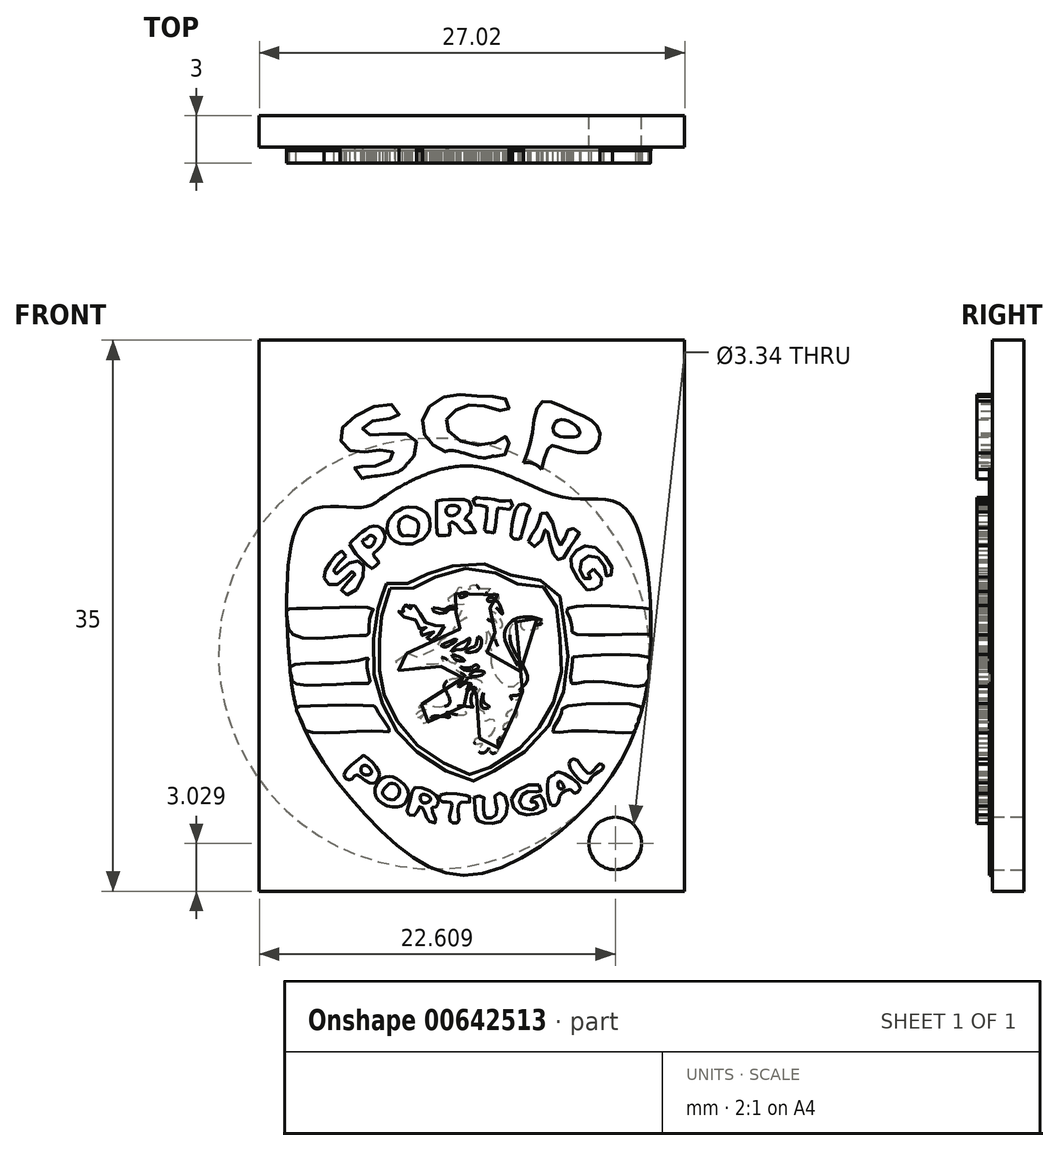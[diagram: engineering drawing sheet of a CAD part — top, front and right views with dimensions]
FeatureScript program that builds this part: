
annotation { "Feature Type Name" : "Feature", "Feature Type Description" : "" }
export const myFeature = defineFeature(function(context is Context, id is Id, definition is map)
    precondition{}
    {
        {
            var Q0;
            Q0=qCreatedBy(makeId("Front.planeOp"),FACE);
            var sketch = newSketch(context, id + "F0", { "sketchPlane" : qUnion([Q0])});
            skLineSegment(sketch, "E0.bottom", {"start": v(-15.43, 13.7) * mm, "end": v(11.59, 13.7) * mm});
            skLineSegment(sketch, "E0.top", {"start": v(-15.43, -21.3) * mm, "end": v(11.59, -21.3) * mm});
            skLineSegment(sketch, "E0.left", {"start": v(-15.43, 13.7) * mm, "end": v(-15.43, -21.3) * mm});
            skPoint(sketch, "E1", {"position": v(11.59, 13.7) * mm});
            skPoint(sketch, "E2", {"position": v(11.59, -21.3) * mm});
            skLineSegment(sketch, "E3", {"start": v(11.59, 13.7) * mm, "end": v(11.59, -21.3) * mm});
            skSolve(sketch);
        }
        {
            var Q0;
            Q0=qCreatedBy(makeId("Front.planeOp"),FACE);
            var sketch = newSketch(context, id + "F1", { "sketchPlane" : qUnion([Q0])});
            skPoint(sketch, "E4.8.internal.snap0", {"position": v(-2.05, -20.29) * mm});
            skFitSpline(sketch, "E4", {"points": [v(-2.05, -20.29) * mm, v(-7.51, -17.64) * mm, v(-12.5, -11.15) * mm, v(-13.53, -6.65) * mm, v(-13.53, 0) * mm, v(-12, 2.96) * mm, v(-8.89, 3.08) * mm, v(-7.39, 3.83) * mm, v(-2.05, 5.7) * mm, v(4.05, 3.69) * mm, v(7.76, 3.09) * mm, v(9.43, -5.8) * mm, v(8.1, -11.92) * mm, v(4.82, -16.5) * mm, v(-2.05, -20.29) * mm]});
            skFitSpline(sketch, "E5", {"points": [v(0, 5.24) * mm, v(-0.48, 6.3) * mm, v(-1.26, 6.22) * mm, v(-3.59, 6.58) * mm, v(-3.52, 5.57) * mm, v(-3.41, 5.6) * mm], "startDerivative": vector(-1.88, 6.53) * mm, "endDerivative": vector(1.52, 1.28) * mm});
            skFitSpline(sketch, "E6", {"points": [v(-5.78, 4.77) * mm, v(-5.98, 5.9) * mm, v(-6.5, 5.4) * mm, v(-8.86, 4.89) * mm, v(-7.39, 3.83) * mm], "startDerivative": vector(-0.76, 7.58) * mm, "endDerivative": vector(8.87, -4.6) * mm});
            skFitSpline(sketch, "E7", {"points": [v(1.07, 4.8) * mm, v(1.36, 5.9) * mm, v(2.48, 5.47) * mm, v(2, 4.39) * mm], "startDerivative": vector(-0.1, 4.46) * mm, "endDerivative": vector(-2.87, -3.44) * mm});
            skFitSpline(sketch, "E8", {"points": [v(-8.86, 4.89) * mm, v(-9.37, 5.65) * mm, v(-8.86, 5.68) * mm, v(-7.7, 5.8) * mm, v(-6.85, 6.44) * mm, v(-7.46, 6.72) * mm, v(-8.86, 6.6) * mm, v(-10.04, 6.93) * mm, v(-10.24, 7.95) * mm, v(-8.86, 9.14) * mm, v(-6.9, 9.55) * mm, v(-6.6, 8.84) * mm, v(-7.8, 8.68) * mm, v(-8.86, 8.1) * mm, v(-8.53, 7.72) * mm, v(-6.6, 7.77) * mm, v(-5.47, 7.33) * mm, v(-5.7, 6.19) * mm, v(-5.98, 5.9) * mm], "startDerivative": vector(-16.53, 19.1) * mm, "endDerivative": vector(-8.11, -5.5) * mm});
            skFitSpline(sketch, "E9", {"points": [v(-3.59, 6.58) * mm, v(-4.82, 7.47) * mm, v(-4.91, 9.07) * mm, v(-3.26, 10.2) * mm, v(-1.08, 10.11) * mm, v(0.3, 9.9) * mm, v(0.33, 9.22) * mm, v(-1.14, 9.53) * mm, v(-2.8, 9.34) * mm, v(-3.59, 8.42) * mm, v(-2.58, 7.26) * mm, v(-0.31, 7.26) * mm, v(0.33, 7.57) * mm, v(0.3, 6.58) * mm, v(-0.48, 6.3) * mm], "startDerivative": vector(-19.26, 9.32) * mm, "endDerivative": vector(-16.98, -0.4) * mm});
            skFitSpline(sketch, "E10", {"points": [v(1.36, 5.9) * mm, v(1.9, 7.72) * mm, v(2.51, 9.77) * mm, v(4.5, 9.16) * mm, v(5.88, 8.42) * mm, v(6.2, 7.38) * mm, v(5.49, 6.58) * mm, v(3.68, 6.86) * mm, v(3.06, 6.98) * mm, v(2.48, 5.47) * mm], "startDerivative": vector(5.01, 12.88) * mm, "endDerivative": vector(-4.42, -17.6) * mm});
            skFitSpline(sketch, "E11", {"points": [v(3.55, 8.6) * mm, v(3.28, 7.84) * mm, v(4.26, 7.53) * mm, v(4.9, 7.72) * mm, v(4.72, 8.2) * mm, v(3.55, 8.6) * mm]});
            skSolve(sketch);
        }
        {
            var Q0;
            Q0 = qSketchRegion(id + "F0", true);
            extrude(context, id + "F2", {"entities" : qUnion([Q0]), "oppositeDirection" : true, "depth" : 2 * mm, "offsetDistance" : 25 * mm});
        }
        {
            var Q0;
            {var subQ0=sQuery(id+"F1.wireOp",EDGE,"E8");Q0=makeQuery(id+"F1.imprint","IMPRINT",FACE,{"disambiguationData":[TD([[makeQuery(id+"F1.imprint","IMPRINT",EDGE,{"derivedFrom":subQ0}),-1.0]])]});}
            var Q1;
            {var subQ0=sQuery(id+"F1.wireOp",EDGE,"E9");Q1=makeQuery(id+"F1.imprint","IMPRINT",FACE,{"disambiguationData":[TD([[makeQuery(id+"F1.imprint","IMPRINT",EDGE,{"derivedFrom":subQ0}),-1.0]])]});}
            var Q2;
            {var subQ0=sQuery(id+"F1.wireOp",EDGE,"E10");Q2=makeQuery(id+"F1.imprint","IMPRINT",FACE,{"disambiguationData":[TD([[makeQuery(id+"F1.imprint","IMPRINT",EDGE,{"derivedFrom":subQ0}),-1.0]])]});}
            extrude(context, id + "F3", {"entities" : qUnion([Q0, Q1, Q2]), "operationType" : NewBodyOperationType.ADD, "depth" : 1 * mm, "offsetDistance" : 25 * mm});
        }
        {
            var Q0;
            {var subQ0=sQuery(id+"F0.wireOp",EDGE,"E0.left");var subQ1=sQuery(id+"F0.wireOp",EDGE,"E0.top");var subQ2=sQuery(id+"F0.wireOp",EDGE,"E0.right");var subQ3=sQuery(id+"F0.wireOp",EDGE,"E0.bottom");Q0=makeQuery(id+"F3.boolean.opBoolean","SPLIT",FACE,{"disambiguationData":[TD([makeQuery(id+"F2.opExtrude","SWEPT_FACE",FACE,{"disambiguationData":[OSD([subQ3])]})])],"derivedFrom":makeQuery(id+"F2.opExtrude","CAP_FACE",FACE,{"disambiguationData":[OSD([subQ3,subQ1,subQ0,subQ2])],"isStart":true})});}
            var sketch = newSketch(context, id + "F4", { "sketchPlane" : qUnion([Q0])});
            skFitSpline(sketch, "E12", {"points": [v(-9.92, 0) * mm, v(-10.21, 0.3) * mm, v(-10.74, -0.17) * mm, v(-11.2, -0.84) * mm, v(-11.3, -1.5) * mm, v(-10.72, -1.9) * mm, v(-9.86, -1.29) * mm, v(-9.46, -1) * mm, v(-9.38, -1.27) * mm, v(-10.21, -2.15) * mm, v(-9.76, -2.47) * mm, v(-8.8, -1.2) * mm, v(-9, -0.4) * mm, v(-9.72, -0.47) * mm, v(-10.37, -1.04) * mm, v(-10.62, -1.14) * mm, v(-10.67, -0.8) * mm, v(-9.92, 0) * mm]});
            skFitSpline(sketch, "E13", {"points": [v(-9.7, 0.77) * mm, v(-8.36, -0.78) * mm, v(-8.28, -0.8) * mm, v(-8.1, -0.67) * mm, v(-7.83, -0.46) * mm, v(-7.94, -0.25) * mm, v(-8.08, -0.13) * mm, v(-8.15, 0) * mm, v(-8.2, 0.08) * mm, v(-7.96, 0.34) * mm, v(-7.75, 0.52) * mm, v(-7.6, 0.72) * mm, v(-7.5, 0.93) * mm, v(-7.44, 1.32) * mm, v(-7.56, 1.59) * mm, v(-7.7, 1.76) * mm, v(-7.92, 1.87) * mm, v(-8.19, 1.9) * mm, v(-8.45, 1.84) * mm, v(-8.63, 1.7) * mm, v(-8.89, 1.53) * mm, v(-8.97, 1.45) * mm, v(-9.18, 1.3) * mm, v(-9.33, 1.13) * mm, v(-9.51, 0.97) * mm, v(-9.7, 0.77) * mm]});
            skFitSpline(sketch, "E14", {"points": [v(-8.87, 0.97) * mm, v(-8.85, 0.82) * mm, v(-8.67, 0.63) * mm, v(-8.56, 0.56) * mm, v(-8.36, 0.57) * mm, v(-8.26, 0.67) * mm, v(-8.16, 0.8) * mm, v(-8.07, 1) * mm, v(-8.07, 1.14) * mm, v(-8.32, 1.29) * mm, v(-8.41, 1.29) * mm, v(-8.54, 1.21) * mm, v(-8.62, 1.05) * mm, v(-8.74, 1.05) * mm, v(-8.8, 1.03) * mm, v(-8.87, 0.97) * mm]});
            skFitSpline(sketch, "E15", {"points": [v(-5.97, 3.09) * mm, v(-6.25, 3.06) * mm, v(-6.48, 2.96) * mm, v(-6.6, 2.82) * mm, v(-6.8, 2.75) * mm, v(-6.9, 2.6) * mm, v(-7.09, 2.47) * mm, v(-7.24, 2.15) * mm, v(-7.28, 2.03) * mm, v(-7.3, 1.82) * mm, v(-7.32, 1.66) * mm, v(-7.26, 1.43) * mm, v(-7.14, 1.2) * mm, v(-6.96, 1.05) * mm, v(-6.76, 0.88) * mm, v(-6.44, 0.77) * mm, v(-6.07, 0.75) * mm, v(-5.66, 0.77) * mm, v(-5.43, 0.89) * mm, v(-5.1, 1.03) * mm, v(-4.86, 1.29) * mm, v(-4.73, 1.4) * mm, v(-4.6, 1.72) * mm, v(-4.58, 2.03) * mm, v(-4.61, 2.34) * mm, v(-4.77, 2.68) * mm, v(-5.04, 2.88) * mm, v(-5.35, 3.03) * mm, v(-5.97, 3.09) * mm]});
            skFitSpline(sketch, "E16", {"points": [v(-6.06, 2.53) * mm, v(-6.5, 2.25) * mm, v(-6.57, 1.99) * mm, v(-6.55, 1.59) * mm, v(-6.34, 1.29) * mm, v(-5.88, 1.29) * mm, v(-5.47, 1.29) * mm, v(-5.33, 1.77) * mm, v(-5.34, 2.1) * mm, v(-5.61, 2.35) * mm, v(-5.97, 2.5) * mm, v(-6.06, 2.53) * mm]});
            skFitSpline(sketch, "E17", {"points": [v(-4.18, 3.5) * mm, v(-4.06, 1.29) * mm, v(-3.97, 1.29) * mm, v(-3.89, 1.29) * mm], "startDerivative": vector(-0.03, -4.4) * mm, "endDerivative": vector(0.58, -0.07) * mm});
            skFitSpline(sketch, "E18", {"points": [v(-3.89, 1.29) * mm, v(-3.59, 1.29) * mm, v(-3.4, 1.29) * mm, v(-3.3, 1.66) * mm, v(-3.38, 2.1) * mm, v(-3.16, 2.15) * mm, v(-2.81, 1.87) * mm, v(-2.45, 1.45) * mm, v(-2.13, 1.47) * mm, v(-1.7, 1.47) * mm, v(-1.79, 1.7) * mm, v(-1.96, 1.94) * mm, v(-2.13, 2.18) * mm, v(-2.38, 2.31) * mm, v(-2.28, 2.5) * mm, v(-2, 2.75) * mm, v(-2.02, 3.27) * mm, v(-2.22, 3.53) * mm, v(-2.99, 3.58) * mm, v(-3.69, 3.57) * mm, v(-4.18, 3.5) * mm], "startDerivative": vector(6.92, 0.45) * mm, "endDerivative": vector(-8.3, -1.8) * mm});
            skFitSpline(sketch, "E19", {"points": [v(-3.47, 3.09) * mm, v(-3.46, 2.6) * mm, v(-2.86, 2.69) * mm, v(-2.78, 3.09) * mm, v(-3.47, 3.09) * mm]});
            skFitSpline(sketch, "E20", {"points": [v(-0.97, 3.09) * mm, v(-1.13, 1.59) * mm, v(-1.03, 1.52) * mm, v(-0.98, 1.51) * mm, v(-0.86, 1.51) * mm, v(-0.77, 1.5) * mm, v(-0.7, 1.48) * mm, v(-0.6, 1.47) * mm, v(-0.56, 1.47) * mm, v(-0.5, 1.47) * mm, v(-0.3, 3.09) * mm, v(-0.24, 3.01) * mm, v(0.16, 3) * mm, v(0.6, 2.99) * mm, v(0.6, 3.5) * mm, v(0.31, 3.5) * mm, v(-0.13, 3.5) * mm, v(-0.49, 3.58) * mm, v(-1, 3.64) * mm, v(-1.36, 3.66) * mm, v(-1.79, 3.68) * mm, v(-1.8, 3.31) * mm, v(-1.5, 3.17) * mm, v(-0.97, 3.09) * mm]});
            skFitSpline(sketch, "E21", {"points": [v(1.07, 3.23) * mm, v(0.57, 1.58) * mm, v(0.55, 1.29) * mm, v(0.63, 1.17) * mm, v(0.78, 1.05) * mm, v(0.96, 1.05) * mm, v(1.1, 1.05) * mm, v(1.22, 1.29) * mm, v(1.33, 1.69) * mm, v(1.45, 2.16) * mm, v(1.67, 2.8) * mm, v(1.76, 3.09) * mm, v(1.07, 3.23) * mm]});
            skFitSpline(sketch, "E22", {"points": [v(1.66, 0.9) * mm, v(2.01, 1.5) * mm, v(2.35, 2.22) * mm, v(2.52, 2.73) * mm, v(3.02, 2.51) * mm, v(3.66, 0.7) * mm, v(4.07, 1.37) * mm, v(4.34, 1.76) * mm, v(4.89, 1.47) * mm, v(4.57, 0.98) * mm, v(3.78, -0.23) * mm, v(3.44, -0.16) * mm, v(3.07, 0.72) * mm, v(2.76, 1.71) * mm, v(2.23, 0.62) * mm, v(1.66, 0.9) * mm]});
            skFitSpline(sketch, "E23", {"points": [v(5.8, -0.84) * mm, v(6.39, -1.76) * mm, v(6.13, -1.9) * mm, v(5.64, -2.25) * mm, v(4.58, -1.13) * mm, v(4.34, -0.18) * mm, v(4.84, 0.44) * mm, v(5.7, 0.62) * mm, v(6.85, -0.5) * mm, v(6.96, -1.16) * mm, v(6.67, -1.35) * mm, v(6.49, -0.64) * mm, v(5.8, 0) * mm, v(5.1, -0.23) * mm, v(4.94, -0.9) * mm, v(5.33, -1.52) * mm, v(5.62, -1.4) * mm, v(5.47, -1.1) * mm, v(5.8, -0.84) * mm]});
            skFitSpline(sketch, "E24", {"points": [v(-10.06, -13.92) * mm, v(-8.9, -12.76) * mm, v(-8.8, -12.68) * mm, v(-7.95, -13.48) * mm, v(-7.85, -14.11) * mm, v(-8.34, -14.46) * mm, v(-9.26, -13.92) * mm, v(-9.64, -14.22) * mm, v(-10.06, -13.92) * mm]});
            skFitSpline(sketch, "E25", {"points": [v(-8.78, -13.31) * mm, v(-8.3, -13.7) * mm, v(-8.57, -13.93) * mm, v(-8.98, -13.66) * mm, v(-8.78, -13.31) * mm]});
            skFitSpline(sketch, "E26", {"points": [v(-7.16, -14) * mm, v(-6.52, -14.3) * mm, v(-6, -14.83) * mm, v(-6.09, -15.59) * mm, v(-6.73, -15.97) * mm, v(-7.8, -15.6) * mm, v(-8.1, -14.9) * mm, v(-7.77, -14.25) * mm, v(-7.16, -14) * mm]});
            skFitSpline(sketch, "E27", {"points": [v(-7.37, -14.67) * mm, v(-7.04, -14.44) * mm, v(-6.55, -14.76) * mm, v(-6.68, -15.34) * mm, v(-7.2, -15.47) * mm, v(-7.61, -15.04) * mm, v(-7.37, -14.67) * mm]});
            skFitSpline(sketch, "E28", {"points": [v(-5.54, -14.73) * mm, v(-4.23, -15.17) * mm, v(-4.06, -15.61) * mm, v(-4.22, -15.96) * mm, v(-4.48, -16.03) * mm, v(-4.2, -16.92) * mm, v(-4.72, -16.8) * mm, v(-4.92, -16.23) * mm, v(-5.25, -15.93) * mm, v(-5.54, -16.47) * mm, v(-6.04, -16.34) * mm, v(-5.86, -15.63) * mm, v(-5.54, -14.73) * mm]});
            skFitSpline(sketch, "E29", {"points": [v(-5.1, -15.17) * mm, v(-4.56, -15.38) * mm, v(-4.73, -15.66) * mm, v(-5.15, -15.59) * mm, v(-5.1, -15.17) * mm]});
            skFitSpline(sketch, "E30", {"points": [v(-3.93, -15.2) * mm, v(-2.06, -15.31) * mm, v(-2.07, -15.38) * mm, v(-2.07, -15.66) * mm, v(-2.63, -15.66) * mm, v(-2.79, -16.42) * mm, v(-2.8, -16.92) * mm, v(-3.28, -16.92) * mm, v(-3.26, -16.13) * mm, v(-3.26, -15.66) * mm, v(-3.85, -15.61) * mm, v(-3.93, -15.2) * mm]});
            skFitSpline(sketch, "E31", {"points": [v(-1.8, -15.34) * mm, v(-1.19, -15.31) * mm, v(-1.19, -15.66) * mm, v(-1.16, -16.33) * mm, v(-1.04, -16.63) * mm, v(-0.46, -16.54) * mm, v(-0.37, -15.96) * mm, v(-0.41, -15.18) * mm, v(0.1, -15.17) * mm, v(0.12, -16.69) * mm, v(-1.01, -16.99) * mm, v(-1.66, -16.67) * mm, v(-1.74, -15.66) * mm, v(-1.8, -15.34) * mm]});
            skFitSpline(sketch, "E32", {"points": [v(2.32, -14.56) * mm, v(2.42, -14.98) * mm, v(1.75, -14.94) * mm, v(1.17, -15.34) * mm, v(1.22, -15.96) * mm, v(2.2, -16.01) * mm, v(2.18, -15.66) * mm, v(1.86, -15.66) * mm, v(1.85, -15.46) * mm, v(2.52, -15.23) * mm, v(2.63, -15.66) * mm, v(2.8, -16.09) * mm, v(1.67, -16.44) * mm, v(0.82, -16.14) * mm, v(0.69, -15.14) * mm, v(2.32, -14.56) * mm]});
            skFitSpline(sketch, "E33", {"points": [v(3.13, -15.86) * mm, v(2.98, -14.08) * mm, v(3.28, -13.93) * mm, v(3.48, -13.74) * mm, v(4.95, -14.73) * mm, v(4.56, -15.08) * mm, v(4.34, -14.84) * mm, v(3.66, -15.24) * mm, v(3.58, -15.66) * mm, v(3.13, -15.86) * mm]});
            skFitSpline(sketch, "E34", {"points": [v(3.58, -14.73) * mm, v(3.9, -14.73) * mm, v(3.63, -14.33) * mm, v(3.58, -14.73) * mm]});
            skFitSpline(sketch, "E35", {"points": [v(4.25, -13.22) * mm, v(5.3, -14.44) * mm, v(5.74, -14) * mm, v(6.42, -13.45) * mm, v(6.21, -13.21) * mm, v(5.52, -13.84) * mm, v(4.67, -12.94) * mm, v(4.25, -13.22) * mm]});
            skSolve(sketch);
        }
        {
            var Q0;
            Q0 = qSketchRegion(id + "F4", true);
            extrude(context, id + "F5", {"entities" : qUnion([Q0]), "operationType" : NewBodyOperationType.ADD, "depth" : 1 * mm, "offsetDistance" : 25 * mm});
        }
        {
            var Q0;
            {var subQ3=sQuery(id+"F0.wireOp",EDGE,"E0.left");var subQ7=sQuery(id+"F0.wireOp",EDGE,"E0.top");var subQ11=sQuery(id+"F0.wireOp",EDGE,"E0.right");var subQ14=sQuery(id+"F0.wireOp",EDGE,"E0.bottom");var subQ15=makeQuery(id+"F2.opExtrude","SWEPT_FACE",FACE,{"disambiguationData":[OSD([subQ14])]});Q0=makeQuery(id+"F5.boolean.opBoolean","SPLIT",FACE,{"disambiguationData":[TD([subQ15])],"derivedFrom":makeQuery(id+"F3.boolean.opBoolean","SPLIT",FACE,{"disambiguationData":[TD([subQ15])],"derivedFrom":makeQuery(id+"F2.opExtrude","CAP_FACE",FACE,{"disambiguationData":[OSD([subQ14,subQ7,subQ3,subQ11])],"isStart":true})})});}
            var sketch = newSketch(context, id + "F6", { "sketchPlane" : qUnion([Q0])});
            skFitSpline(sketch, "E36", {"points": [v(-12.36, -3.34) * mm, v(-8.22, -3.38) * mm, v(-8.4, -3.83) * mm, v(-8.48, -4.95) * mm, v(-9.02, -5.05) * mm, v(-13.26, -5.03) * mm, v(-13.66, -3.98) * mm, v(-13.68, -3.47) * mm, v(-12.36, -3.34) * mm]});
            skFitSpline(sketch, "E37", {"points": [v(-9.84, -6.75) * mm, v(-8.5, -6.52) * mm, v(-8.62, -6.84) * mm, v(-8.4, -8) * mm, v(-9.06, -8.11) * mm, v(-13.22, -8.1) * mm, v(-13.41, -7.58) * mm, v(-13.46, -7.02) * mm, v(-9.84, -6.75) * mm]});
            skFitSpline(sketch, "E38", {"points": [v(-12.88, -9.58) * mm, v(-8.03, -9.58) * mm, v(-8.01, -9.7) * mm, v(-7.15, -11.09) * mm, v(-7.87, -11.13) * mm, v(-12.38, -11.15) * mm, v(-12.68, -10.67) * mm, v(-13.04, -9.86) * mm, v(-13.08, -9.68) * mm, v(-12.88, -9.58) * mm]});
            skFitSpline(sketch, "E39", {"points": [v(4.14, -3.35) * mm, v(9.36, -3.37) * mm, v(9.41, -3.46) * mm, v(9.41, -4.99) * mm, v(9.26, -4.99) * mm, v(4.52, -4.92) * mm, v(4.44, -4.6) * mm, v(4.37, -4.21) * mm, v(4.25, -3.83) * mm, v(4.14, -3.35) * mm]});
            skFitSpline(sketch, "E40", {"points": [v(9.33, -6.47) * mm, v(4.47, -6.44) * mm, v(4.47, -6.55) * mm, v(4.36, -8.04) * mm, v(5.04, -8.04) * mm, v(7.43, -8.15) * mm, v(9.23, -8.1) * mm, v(9.28, -7.17) * mm, v(9.28, -7.07) * mm, v(9.33, -6.82) * mm, v(9.33, -6.47) * mm]});
            skFitSpline(sketch, "E41", {"points": [v(8.86, -9.58) * mm, v(3.86, -9.63) * mm, v(3.79, -9.82) * mm, v(3.66, -10.24) * mm, v(3.2, -11.16) * mm, v(4.5, -11.1) * mm, v(8.32, -11.2) * mm, v(8.49, -10.97) * mm, v(8.51, -10.73) * mm, v(8.67, -10.58) * mm, v(8.65, -10.44) * mm, v(8.67, -10.25) * mm, v(8.74, -10.15) * mm, v(8.82, -9.97) * mm, v(8.83, -9.86) * mm, v(8.86, -9.58) * mm]});
            skSolve(sketch);
        }
        {
            var Q0;
            Q0=makeQuery(id+"F6.imprint","IMPRINT",FACE,{"disambiguationData":[TD([[makeQuery(id+"F6.imprint","IMPRINT",EDGE,{"derivedFrom":sQuery(id+"F6.wireOp",EDGE,"E38")}),-1.0]])]});
            var Q1;
            {var subQ0=sQuery(id+"F6.wireOp",EDGE,"E37");var subQ1=makeQuery(id+"F2.opExtrude","CAP_EDGE",EDGE,{"disambiguationData":[OSD([sQuery(id+"F0.wireOp",EDGE,"E0.left")])],"isStart":true});var subQ2=makeQuery(id+"F6.imprint","INTERSECT",VERTEX,{"disambiguationData":[OD(0.0)],"derivedFrom":[subQ1,subQ0]});Q1=makeQuery(id+"F6.imprint","IMPRINT",FACE,{"disambiguationData":[TD([[makeQuery(id+"F6.imprint","IMPRINT",EDGE,{"disambiguationData":[TD([[subQ2,1.0]])],"derivedFrom":subQ0}),-1.0]])]});}
            var Q2;
            {var subQ0=sQuery(id+"F6.wireOp",EDGE,"E36");var subQ1=makeQuery(id+"F2.opExtrude","CAP_EDGE",EDGE,{"disambiguationData":[OSD([sQuery(id+"F0.wireOp",EDGE,"E0.left")])],"isStart":true});var subQ2=makeQuery(id+"F6.imprint","INTERSECT",VERTEX,{"disambiguationData":[OD(0.0)],"derivedFrom":[subQ1,subQ0]});Q2=makeQuery(id+"F6.imprint","IMPRINT",FACE,{"disambiguationData":[TD([[makeQuery(id+"F6.imprint","IMPRINT",EDGE,{"disambiguationData":[TD([[subQ2,-1.0]])],"derivedFrom":subQ0}),-1.0]])]});}
            var Q3;
            Q3=makeQuery(id+"F6.imprint","IMPRINT",FACE,{"disambiguationData":[TD([[makeQuery(id+"F6.imprint","IMPRINT",EDGE,{"derivedFrom":sQuery(id+"F6.wireOp",EDGE,"E40")}),1.0]])]});
            var Q4;
            Q4=makeQuery(id+"F6.imprint","IMPRINT",FACE,{"disambiguationData":[TD([[makeQuery(id+"F6.imprint","IMPRINT",EDGE,{"derivedFrom":sQuery(id+"F6.wireOp",EDGE,"E41")}),1.0]])]});
            var Q5;
            Q5=makeQuery(id+"F6.imprint","IMPRINT",FACE,{"disambiguationData":[TD([[makeQuery(id+"F6.imprint","IMPRINT",EDGE,{"derivedFrom":sQuery(id+"F6.wireOp",EDGE,"E39")}),-1.0]])]});
            extrude(context, id + "F7", {"entities" : qUnion([Q0, Q1, Q2, Q3, Q4, Q5]), "operationType" : NewBodyOperationType.ADD, "depth" : 1 * mm, "offsetDistance" : 25 * mm});
        }
        {
            var Q0;
            {var subQ3=sQuery(id+"F0.wireOp",EDGE,"E0.left");var subQ18=sQuery(id+"F0.wireOp",EDGE,"E0.top");var subQ23=sQuery(id+"F0.wireOp",EDGE,"E0.right");var subQ27=sQuery(id+"F0.wireOp",EDGE,"E0.bottom");var subQ28=makeQuery(id+"F2.opExtrude","SWEPT_FACE",FACE,{"disambiguationData":[OSD([subQ27])]});Q0=makeQuery(id+"F7.boolean.opBoolean","SPLIT",FACE,{"disambiguationData":[TD([subQ28])],"derivedFrom":makeQuery(id+"F5.boolean.opBoolean","SPLIT",FACE,{"disambiguationData":[TD([subQ28])],"derivedFrom":makeQuery(id+"F3.boolean.opBoolean","SPLIT",FACE,{"disambiguationData":[TD([subQ28])],"derivedFrom":makeQuery(id+"F2.opExtrude","CAP_FACE",FACE,{"disambiguationData":[OSD([subQ27,subQ18,subQ3,subQ23])],"isStart":true})})})});}
            var sketch = newSketch(context, id + "F8", { "sketchPlane" : qUnion([Q0])});
            skFitSpline(sketch, "E42", {"points": [v(-7.37, -1.77) * mm, v(-6.23, -1.77) * mm, v(-5.05, -1.31) * mm, v(-3.57, -0.74) * mm, v(-0.95, -0.55) * mm, v(1.03, -1.39) * mm, v(3.23, -1.85) * mm, v(3.88, -4) * mm, v(4.18, -6.21) * mm, v(3.6, -9.55) * mm, v(1.6, -12.29) * mm, v(-1.02, -13.96) * mm, v(-2.05, -14.3) * mm, v(-4.63, -13) * mm, v(-6.42, -11.5) * mm, v(-7.63, -9.33) * mm, v(-8.2, -6.86) * mm, v(-7.97, -3.7) * mm, v(-7.7, -2.76) * mm, v(-7.6, -2.41) * mm, v(-7.55, -2.15) * mm, v(-7.37, -1.77) * mm]});
            skFitSpline(sketch, "E43", {"points": [v(-7.14, -2.1) * mm, v(-5.93, -2.07) * mm, v(-4.85, -1.68) * mm, v(-3.23, -0.95) * mm, v(-0.98, -0.91) * mm, v(0.32, -1.45) * mm, v(1.59, -1.95) * mm, v(2.94, -2.07) * mm, v(3.5, -3.58) * mm, v(3.72, -5.86) * mm, v(3.66, -8.18) * mm, v(2.85, -10.07) * mm, v(1.92, -11.4) * mm, v(0.34, -12.79) * mm, v(-1.66, -13.84) * mm, v(-2.1, -13.9) * mm, v(-3.78, -13.15) * mm, v(-5.48, -11.95) * mm, v(-6.86, -10.2) * mm, v(-7.58, -8.6) * mm, v(-7.79, -7.32) * mm, v(-7.8, -5.46) * mm, v(-7.75, -4.24) * mm, v(-7.4, -2.91) * mm, v(-7.32, -2.69) * mm, v(-7.29, -2.48) * mm, v(-7.22, -2.3) * mm, v(-7.14, -2.1) * mm]});
            skSolve(sketch);
        }
        {
            var Q0;
            Q0=makeQuery(id+"F8.imprint","IMPRINT",FACE,{"disambiguationData":[TD([[makeQuery(id+"F8.imprint","IMPRINT",EDGE,{"derivedFrom":sQuery(id+"F8.wireOp",EDGE,"E42")}),-1.0]])]});
            extrude(context, id + "F9", {"entities" : qUnion([Q0]), "operationType" : NewBodyOperationType.ADD, "depth" : 1 * mm, "offsetDistance" : 25 * mm});
        }
        {
            var Q0;
            {var subQ3=sQuery(id+"F0.wireOp",EDGE,"E0.left");var subQ20=sQuery(id+"F0.wireOp",EDGE,"E0.top");var subQ26=sQuery(id+"F0.wireOp",EDGE,"E0.right");var subQ30=sQuery(id+"F0.wireOp",EDGE,"E0.bottom");var subQ31=makeQuery(id+"F2.opExtrude","SWEPT_FACE",FACE,{"disambiguationData":[OSD([subQ30])]});Q0=makeQuery(id+"F9.boolean.opBoolean","SPLIT",FACE,{"disambiguationData":[TD([subQ31])],"derivedFrom":makeQuery(id+"F7.boolean.opBoolean","SPLIT",FACE,{"disambiguationData":[TD([subQ31])],"derivedFrom":makeQuery(id+"F5.boolean.opBoolean","SPLIT",FACE,{"disambiguationData":[TD([subQ31])],"derivedFrom":makeQuery(id+"F3.boolean.opBoolean","SPLIT",FACE,{"disambiguationData":[TD([subQ31])],"derivedFrom":makeQuery(id+"F2.opExtrude","CAP_FACE",FACE,{"disambiguationData":[OSD([subQ30,subQ20,subQ3,subQ26])],"isStart":true})})})})});}
            var sketch = newSketch(context, id + "F10", { "sketchPlane" : qUnion([Q0])});
            skFitSpline(sketch, "E44", {"points": [v(-3.67, -4.45) * mm, v(-4.36, -4.42) * mm, v(-5, -4.1) * mm, v(-5.38, -3.37) * mm, v(-5.72, -3.12) * mm, v(-5.87, -3.12) * mm, v(-5.73, -3.38) * mm, v(-5.96, -3.23) * mm, v(-6.15, -3.14) * mm, v(-6.38, -3.23) * mm, v(-6.13, -3.52) * mm, v(-6.38, -3.54) * mm, v(-6.57, -3.48) * mm, v(-6.49, -3.77) * mm, v(-5.6, -4.03) * mm, v(-5.27, -4.4) * mm, v(-5.4, -4.52) * mm, v(-5.29, -4.63) * mm, v(-4.9, -4.54) * mm, v(-4.8, -4.62) * mm, v(-5.29, -4.9) * mm, v(-5.12, -5.06) * mm, v(-4.67, -4.94) * mm, v(-4.5, -4.8) * mm, v(-4.35, -4.83) * mm, v(-4.8, -5.25) * mm, v(-4.6, -5.37) * mm, v(-4.14, -5.14) * mm, v(-3.67, -4.45) * mm]});
            skFitSpline(sketch, "E45", {"points": [v(-2.96, -2.4) * mm, v(-3.47, -2.55) * mm, v(-3.5, -2.73) * mm, v(-3.35, -2.78) * mm, v(-3.45, -2.9) * mm, v(-3.45, -3.07) * mm, v(-3.08, -3.06) * mm, v(-2.56, -3.01) * mm, v(-2.21, -3.38) * mm, v(-2.7, -3.63) * mm, v(-3.11, -3.63) * mm, v(-2.85, -4.07) * mm, v(-2.5, -3.86) * mm, v(-2.24, -3.9) * mm, v(-2.34, -4.07) * mm, v(-2.59, -4.2) * mm, v(-3.3, -4.52) * mm, v(-3.3, -4.66) * mm, v(-3.02, -4.66) * mm, v(-2.68, -4.64) * mm, v(-3.28, -4.97) * mm, v(-3.94, -5.35) * mm, v(-4.01, -5.71) * mm, v(-4.1, -5.83) * mm, v(-4.79, -6.2) * mm, v(-5.4, -6.47) * mm, v(-5.9, -6.33) * mm, v(-6.3, -6.1) * mm, v(-6.56, -6.22) * mm, v(-6.3, -6.38) * mm, v(-6.18, -6.53) * mm, v(-6.68, -6.64) * mm, v(-6.79, -6.89) * mm, v(-6.57, -6.87) * mm, v(-6.28, -6.78) * mm, v(-6.2, -6.89) * mm, v(-6.43, -7) * mm, v(-6.56, -7.37) * mm, v(-6.18, -7.3) * mm, v(-5.63, -7.01) * mm, v(-5.1, -6.95) * mm, v(-4.74, -7.1) * mm, v(-4.62, -7) * mm, v(-4.85, -6.8) * mm, v(-4.77, -6.66) * mm, v(-4.3, -6.87) * mm, v(-3.64, -7.01) * mm, v(-3.73, -6.8) * mm, v(-4.17, -6.58) * mm, v(-3.81, -6.46) * mm, v(-3.16, -6.78) * mm, v(-2.93, -6.8) * mm, v(-3.08, -7.06) * mm, v(-2.35, -7.63) * mm, v(-2.56, -7.77) * mm, v(-3.25, -7.85) * mm, v(-3.69, -8.2) * mm, v(-3.4, -8.97) * mm, v(-3.4, -9.43) * mm, v(-4.15, -9.62) * mm, v(-4.76, -9.45) * mm, v(-5.2, -9.48) * mm, v(-5.32, -9.64) * mm, v(-4.87, -9.67) * mm, v(-4.9, -9.82) * mm, v(-5.2, -9.85) * mm, v(-5.5, -10.15) * mm, v(-5.46, -10.32) * mm, v(-4.98, -10.05) * mm, v(-5.27, -10.47) * mm, v(-4.73, -10.57) * mm, v(-4.35, -10.18) * mm, v(-3.33, -10.24) * mm, v(-3.53, -9.96) * mm, v(-2.71, -10.12) * mm, v(-2.28, -9.98) * mm, v(-2.76, -9.7) * mm, v(-2.83, -9.54) * mm, v(-1.84, -9.6) * mm, v(-1.95, -9.42) * mm, v(-1.83, -8.63) * mm, v(-1.66, -8.46) * mm, v(-1.76, -8.36) * mm, v(-2.07, -8.46) * mm, v(-2.18, -8.61) * mm, v(-2.26, -8.52) * mm, v(-2.1, -8.3) * mm, v(-1.97, -8.15) * mm, v(-2.35, -8.12) * mm, v(-2.63, -8.3) * mm, v(-2.8, -8.29) * mm, v(-2.66, -8.07) * mm, v(-2.3, -7.96) * mm, v(-2.18, -7.77) * mm, v(-1.72, -7.79) * mm, v(-1.27, -8.04) * mm, v(-1.45, -8.47) * mm, v(-1.69, -9.08) * mm, v(-1.48, -9.71) * mm, v(-1.13, -10) * mm, v(-1.13, -10.5) * mm, v(-0.72, -10.33) * mm, v(-0.45, -10.72) * mm, v(-0.94, -11.57) * mm, v(-1.55, -11.59) * mm, v(-1.8, -11.73) * mm, v(-1.69, -11.93) * mm, v(-1.27, -11.93) * mm, v(-1.5, -12.37) * mm, v(-1.13, -12.5) * mm, v(-0.83, -12.2) * mm, v(-0.72, -12.49) * mm, v(-0.34, -12.46) * mm, v(-0.23, -12.13) * mm, v(-0.26, -11.68) * mm, v(0.27, -11.19) * mm, v(0.31, -10.95) * mm, v(0.11, -11.03) * mm, v(0.14, -10.7) * mm, v(0.6, -10.46) * mm, v(0.97, -10.15) * mm, v(0.94, -9.85) * mm, v(0.66, -10.07) * mm, v(0.28, -10.2) * mm, v(0.36, -9.91) * mm, v(1.01, -9.48) * mm, v(1.1, -9.08) * mm, v(0.81, -9.2) * mm, v(0.52, -8.92) * mm, v(0.9, -8.86) * mm, v(1.3, -8.61) * mm, v(1.1, -8.55) * mm, v(1.52, -8.07) * mm, v(1.37, -7.08) * mm, v(0.62, -5.79) * mm, v(0.49, -5.03) * mm, v(0.66, -4.36) * mm, v(1.12, -4.16) * mm, v(1.15, -4.44) * mm, v(1.5, -4.73) * mm, v(2.11, -4.64) * mm, v(2.3, -4.55) * mm, v(2.2, -4.4) * mm, v(2.5, -4.31) * mm, v(2.32, -4.16) * mm, v(2.56, -4.1) * mm, v(2.22, -3.97) * mm, v(1.85, -3.88) * mm, v(1.25, -3.9) * mm, v(0.64, -4.13) * mm, v(0.16, -4.84) * mm, v(0.38, -5.87) * mm, v(1.12, -7.26) * mm, v(1.12, -7.87) * mm, v(0.6, -8.36) * mm, v(-0.2, -7.9) * mm, v(-0.68, -6.87) * mm, v(-0.7, -5.9) * mm, v(-0.79, -5.82) * mm, v(-0.97, -6.16) * mm, v(-1.03, -5.7) * mm, v(-0.96, -4.98) * mm, v(-1.07, -4.62) * mm, v(-0.83, -4.9) * mm, v(-0.63, -5.56) * mm, v(-0.3, -5.74) * mm, v(-0.4, -5.48) * mm, v(-0.45, -4.67) * mm, v(-0.62, -4.2) * mm, v(-0.93, -4.04) * mm, v(-0.55, -3.97) * mm, v(-0.23, -4.53) * mm, v(0, -4.52) * mm, v(-0.2, -3.88) * mm, v(-0.68, -3.5) * mm, v(-0.79, -3.3) * mm, v(-0.5, -3.23) * mm, v(0, -3.7) * mm, v(-0.18, -3.1) * mm, v(-0.4, -2.87) * mm, v(-0.86, -2.89) * mm, v(-0.94, -2.8) * mm, v(-0.82, -2.64) * mm, v(-0.23, -2.75) * mm, v(-0.38, -2.42) * mm, v(-1.08, -2.42) * mm, v(-0.8, -2.14) * mm, v(-1.45, -2.1) * mm, v(-1.58, -1.91) * mm, v(-2.06, -1.97) * mm, v(-2.06, -2.14) * mm, v(-2.77, -2.03) * mm, v(-2.96, -2.4) * mm]});
            skFitSpline(sketch, "E46", {"points": [v(-4.4, -3.32) * mm, v(-4.26, -3.57) * mm, v(-3.52, -3.57) * mm, v(-3.33, -3.38) * mm, v(-2.88, -3.37) * mm, v(-3.02, -3.28) * mm, v(-3.45, -3.26) * mm, v(-3.66, -3.42) * mm, v(-4.4, -3.32) * mm]});
            skFitSpline(sketch, "E47", {"points": [v(-3.27, -6.1) * mm, v(-2.93, -5.97) * mm, v(-2.42, -5.9) * mm, v(-2.06, -5.25) * mm, v(-2.4, -5.43) * mm, v(-2.82, -5.65) * mm, v(-3.27, -6.1) * mm]});
            skFitSpline(sketch, "E48", {"points": [v(-2.9, -5.3) * mm, v(-3.86, -5.7) * mm, v(-3.75, -5.77) * mm, v(-3.36, -5.7) * mm, v(-2.9, -5.3) * mm]});
            skFitSpline(sketch, "E49", {"points": [v(-2.34, -6.05) * mm, v(-1.84, -5.79) * mm, v(-1.64, -5.65) * mm, v(-1.55, -5.17) * mm, v(-1.36, -5.25) * mm, v(-1.42, -5.87) * mm, v(-2.09, -6.15) * mm, v(-2.34, -6.05) * mm]});
            skFitSpline(sketch, "E50", {"points": [v(-3.18, -6.28) * mm, v(-2.4, -6.64) * mm, v(-2.79, -6.66) * mm, v(-3.07, -6.5) * mm, v(-3.18, -6.28) * mm]});
            skFitSpline(sketch, "E51", {"points": [v(-2.66, -7.06) * mm, v(-2.28, -7.14) * mm, v(-1.83, -7) * mm, v(-1.69, -6.92) * mm, v(-1.5, -7.04) * mm, v(-2.17, -7.3) * mm, v(-2.66, -7.06) * mm]});
            skFitSpline(sketch, "E52", {"points": [v(-2.06, -7.6) * mm, v(-1.47, -7.63) * mm, v(-1.14, -7.39) * mm, v(-1.78, -7.36) * mm, v(-2.06, -7.6) * mm]});
            skFitSpline(sketch, "E53", {"points": [v(-1.2, -8.72) * mm, v(-1.2, -9.25) * mm, v(-0.82, -9.59) * mm, v(-1.14, -9.7) * mm, v(-1.36, -9.34) * mm, v(-1.2, -8.72) * mm]});
            skFitSpline(sketch, "E54", {"points": [v(-2.66, -2.64) * mm, v(-2.17, -2.4) * mm, v(-2.65, -2.4) * mm, v(-2.66, -2.64) * mm]});
            skSolve(sketch);
        }
        {
            var Q0;
            Q0=makeQuery(id+"F10.imprint","IMPRINT",FACE,{"disambiguationData":[TD([[makeQuery(id+"F10.imprint","IMPRINT",EDGE,{"derivedFrom":sQuery(id+"F10.wireOp",EDGE,"E45")}),1.0]])]});
            var Q1;
            Q1=makeQuery(id+"F10.imprint","IMPRINT",FACE,{"disambiguationData":[TD([[makeQuery(id+"F10.imprint","IMPRINT",EDGE,{"derivedFrom":sQuery(id+"F10.wireOp",EDGE,"E44")}),1.0]])]});
            var Q2;
            Q2=makeQuery(id+"F10.imprint","IMPRINT",FACE,{"disambiguationData":[TD([[makeQuery(id+"F10.imprint","IMPRINT",EDGE,{"derivedFrom":sQuery(id+"F10.wireOp",EDGE,"E46")}),1.0]])]});
            extrude(context, id + "F11", {"entities" : qUnion([Q0, Q1, Q2]), "operationType" : NewBodyOperationType.ADD, "depth" : 1 * mm, "offsetDistance" : 25 * mm});
        }
        {
            var Q0;
            {var subQ1=sQuery(id+"F1.wireOp",EDGE,"E4");var subQ6=sQuery(id+"F1.wireOp",EDGE,"E6");var subQ7=makeQuery(id+"F1.imprint","INTERSECT",VERTEX,{"disambiguationData":[OD(0.0)],"derivedFrom":[subQ1,subQ6]});Q0=makeQuery(id+"F1.imprint","IMPRINT",FACE,{"disambiguationData":[TD([[makeQuery(id+"F1.imprint","IMPRINT",EDGE,{"disambiguationData":[TD([[subQ7,1.0]])],"derivedFrom":subQ1}),-1.0]])]});}
            extrude(context, id + "F12", {"entities" : qUnion([Q0]), "operationType" : NewBodyOperationType.ADD, "depth" : 0.2 * mm, "offsetDistance" : 25 * mm});
        }
        {
            var Q0;
            Q0=makeQuery(id+"F2.opExtrude","CAP_FACE",FACE,{"disambiguationData":[OSD([sQuery(id+"F0.wireOp",EDGE,"E0.bottom"),sQuery(id+"F0.wireOp",EDGE,"E0.top"),sQuery(id+"F0.wireOp",EDGE,"E0.left"),sQuery(id+"F0.wireOp",EDGE,"E3")])],"isStart":false});
            var sketch = newSketch(context, id + "F13", { "sketchPlane" : qUnion([Q0])});
            skCircle(sketch, "E55", {"center": v(-7.18, -18.27) * mm, "radius": 1.67 * mm});
            skSolve(sketch);
        }
        {
            var Q0;
            Q0=makeQuery(id+"F13.imprint","IMPRINT",FACE,{"disambiguationData":[TD([[makeQuery(id+"F13.imprint","IMPRINT",EDGE,{"derivedFrom":sQuery(id+"F13.wireOp",EDGE,"E55")}),1.0]])]});
            extrude(context, id + "F14", {"entities" : qUnion([Q0]), "operationType" : NewBodyOperationType.REMOVE, "oppositeDirection" : true, "depth" : 25 * mm, "offsetDistance" : 25 * mm});
        }
    });
